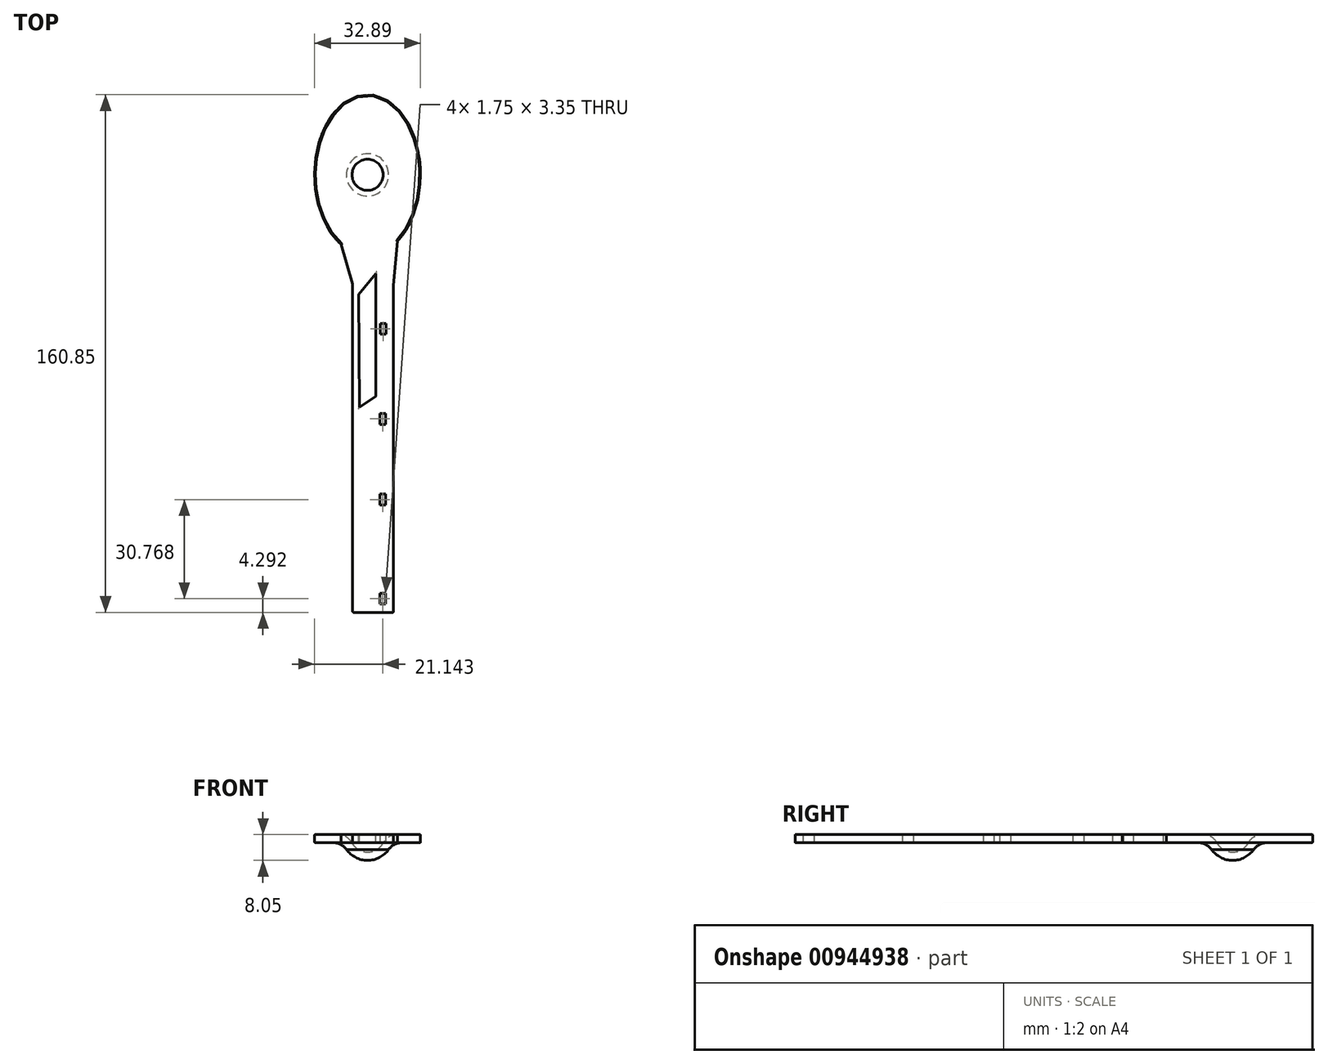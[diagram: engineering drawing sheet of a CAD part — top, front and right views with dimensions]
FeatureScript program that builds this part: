
annotation { "Feature Type Name" : "Feature", "Feature Type Description" : "" }
export const myFeature = defineFeature(function(context is Context, id is Id, definition is map)
    precondition{}
    {
        {
            var Q0;
            Q0=qCreatedBy(makeId("Top.planeOp"),FACE);
            var sketch = newSketch(context, id + "F0", { "sketchPlane" : qUnion([Q0])});
            skEllipticalArc(sketch, "E0", {});
            skLineSegment(sketch, "E1", {"start": v(-8.18, -21.6) * mm, "end": v(-4.62, -33.9) * mm});
            skLineSegment(sketch, "E2", {"start": v(-4.62, -33.9) * mm, "end": v(-4.62, -135.94) * mm});
            skLineSegment(sketch, "E3", {"start": v(-4.62, -135.94) * mm, "end": v(8.08, -135.94) * mm});
            skLineSegment(sketch, "E4", {"start": v(8.08, -135.94) * mm, "end": v(8.08, -34.34) * mm});
            skLineSegment(sketch, "E5", {"start": v(8.08, -34.34) * mm, "end": v(9.27, -20.58) * mm});
            const initialGuessF0  = {"E0": [0, 0, 0, -1, 0.0249080586106296, 0.0164429262639253, 0.5987226395592762, 5.762282687151485]};
            skSetInitialGuess(sketch, initialGuessF0);
            skSolve(sketch);
        }
        {
            var Q0;
            Q0 = qSketchRegion(id + "F0", true);
            extrude(context, id + "F1", {"entities" : qUnion([Q0]), "depth" : 2.54 * mm, "offsetDistance" : 25.4 * mm});
        }
        {
            var Q0;
            Q0=makeQuery(id+"F1.opExtrude","CAP_EDGE",EDGE,{"disambiguationData":[OSD([sQuery(id+"F0.wireOp",EDGE,"E1")])],"isStart":false});
            var Q1;
            Q1=makeQuery(id+"F1.opExtrude","CAP_EDGE",EDGE,{"disambiguationData":[OSD([sQuery(id+"F0.wireOp",EDGE,"E2")])],"isStart":false});
            var Q2;
            Q2=makeQuery(id+"F1.opExtrude","CAP_EDGE",EDGE,{"disambiguationData":[OSD([sQuery(id+"F0.wireOp",EDGE,"E0")])],"isStart":false});
            var Q3;
            Q3=makeQuery(id+"F1.opExtrude","CAP_EDGE",EDGE,{"disambiguationData":[OSD([sQuery(id+"F0.wireOp",EDGE,"E5")])],"isStart":false});
            var Q4;
            Q4=makeQuery(id+"F1.opExtrude","CAP_EDGE",EDGE,{"disambiguationData":[OSD([sQuery(id+"F0.wireOp",EDGE,"E4")])],"isStart":false});
            var Q5;
            Q5=makeQuery(id+"F1.opExtrude","CAP_EDGE",EDGE,{"disambiguationData":[OSD([sQuery(id+"F0.wireOp",EDGE,"E0")])],"isStart":true});
            var Q6;
            Q6=makeQuery(id+"F1.opExtrude","CAP_EDGE",EDGE,{"disambiguationData":[OSD([sQuery(id+"F0.wireOp",EDGE,"E5")])],"isStart":true});
            var Q7;
            Q7=makeQuery(id+"F1.opExtrude","CAP_EDGE",EDGE,{"disambiguationData":[OSD([sQuery(id+"F0.wireOp",EDGE,"E3")])],"isStart":true});
            var Q8;
            Q8=makeQuery(id+"F1.opExtrude","SWEPT_EDGE",EDGE,{"disambiguationData":[OSD([sQuery(id+"F0.wireOp",EDGE,"E3"),sQuery(id+"F0.wireOp",EDGE,"E4")])]});
            var Q9;
            Q9=makeQuery(id+"F1.opExtrude","CAP_EDGE",EDGE,{"disambiguationData":[OSD([sQuery(id+"F0.wireOp",EDGE,"E3")])],"isStart":false});
            var Q10;
            Q10=makeQuery(id+"F1.opExtrude","SWEPT_EDGE",EDGE,{"disambiguationData":[OSD([sQuery(id+"F0.wireOp",EDGE,"E2"),sQuery(id+"F0.wireOp",EDGE,"E3")])]});
            var Q11;
            Q11=makeQuery(id+"F1.opExtrude","CAP_EDGE",EDGE,{"disambiguationData":[OSD([sQuery(id+"F0.wireOp",EDGE,"E4")])],"isStart":true});
            fillet(context, id + "F2", {"entities" : qUnion([Q0, Q1, Q2, Q3, Q4, Q5, Q6, Q7, Q8, Q9, Q10, Q11]), "radius" : 0.25 * mm, "tangentPropagation" : true, "allowEdgeOverflow" : false});
        }
        {
            var Q0;
            Q0=makeQuery(id+"F1.opExtrude","CAP_FACE",FACE,{"disambiguationData":[OSD([sQuery(id+"F0.wireOp",EDGE,"E0"),sQuery(id+"F0.wireOp",EDGE,"E1"),sQuery(id+"F0.wireOp",EDGE,"E2"),sQuery(id+"F0.wireOp",EDGE,"E3"),sQuery(id+"F0.wireOp",EDGE,"E4"),sQuery(id+"F0.wireOp",EDGE,"E5")])],"isStart":false});
            var sketch = newSketch(context, id + "F3", { "sketchPlane" : qUnion([Q0])});
            skLineSegment(sketch, "E6", {"start": v(-2.5, -72.22) * mm, "end": v(2.5, -68.83) * mm});
            skLineSegment(sketch, "E7", {"start": v(2.5, -68.83) * mm, "end": v(2.5, -30.73) * mm});
            skLineSegment(sketch, "E8", {"start": v(2.5, -30.73) * mm, "end": v(-2.82, -37.19) * mm});
            skLineSegment(sketch, "E9", {"start": v(-2.82, -37.19) * mm, "end": v(-2.5, -72.22) * mm});
            skSolve(sketch);
        }
        {
            var Q0;
            Q0 = qSketchRegion(id + "F3", true);
            extrude(context, id + "F4", {"entities" : qUnion([Q0]), "operationType" : NewBodyOperationType.REMOVE, "oppositeDirection" : true, "depth" : 25.4 * mm, "offsetDistance" : 25.4 * mm});
        }
        {
            var Q0;
            Q0=makeQuery(id+"F4.boolean.opBoolean","COPY",EDGE,{"derivedFrom":makeQuery(id+"F4.opExtrude","CAP_EDGE",EDGE,{"disambiguationData":[OSD([sQuery(id+"F3.wireOp",EDGE,"E8")])],"isStart":true})});
            var Q1;
            Q1=makeQuery(id+"F4.boolean.opBoolean","COPY",EDGE,{"derivedFrom":makeQuery(id+"F4.opExtrude","CAP_EDGE",EDGE,{"disambiguationData":[OSD([sQuery(id+"F3.wireOp",EDGE,"E9")])],"isStart":true})});
            var Q2;
            Q2=makeQuery(id+"F4.boolean.opBoolean","COPY",EDGE,{"derivedFrom":makeQuery(id+"F4.opExtrude","CAP_EDGE",EDGE,{"disambiguationData":[OSD([sQuery(id+"F3.wireOp",EDGE,"E7")])],"isStart":true})});
            var Q3;
            Q3=makeQuery(id+"F4.boolean.opBoolean","COPY",EDGE,{"derivedFrom":makeQuery(id+"F4.opExtrude","CAP_EDGE",EDGE,{"disambiguationData":[OSD([sQuery(id+"F3.wireOp",EDGE,"E6")])],"isStart":true})});
            var Q4;
            Q4=makeQuery(id+"F4.boolean.opBoolean","INTERSECT",EDGE,{"derivedFrom":[makeQuery(id+"F1.opExtrude","CAP_FACE",FACE,{"disambiguationData":[OSD([sQuery(id+"F0.wireOp",EDGE,"E0"),sQuery(id+"F0.wireOp",EDGE,"E1"),sQuery(id+"F0.wireOp",EDGE,"E2"),sQuery(id+"F0.wireOp",EDGE,"E3"),sQuery(id+"F0.wireOp",EDGE,"E4"),sQuery(id+"F0.wireOp",EDGE,"E5")])],"isStart":true}),makeQuery(id+"F4.opExtrude","SWEPT_FACE",FACE,{"disambiguationData":[OSD([sQuery(id+"F3.wireOp",EDGE,"E8")])]})]});
            var Q5;
            Q5=makeQuery(id+"F4.boolean.opBoolean","INTERSECT",EDGE,{"derivedFrom":[makeQuery(id+"F1.opExtrude","CAP_FACE",FACE,{"disambiguationData":[OSD([sQuery(id+"F0.wireOp",EDGE,"E0"),sQuery(id+"F0.wireOp",EDGE,"E1"),sQuery(id+"F0.wireOp",EDGE,"E2"),sQuery(id+"F0.wireOp",EDGE,"E3"),sQuery(id+"F0.wireOp",EDGE,"E4"),sQuery(id+"F0.wireOp",EDGE,"E5")])],"isStart":true}),makeQuery(id+"F4.opExtrude","SWEPT_FACE",FACE,{"disambiguationData":[OSD([sQuery(id+"F3.wireOp",EDGE,"E7")])]})]});
            var Q6;
            Q6=makeQuery(id+"F4.boolean.opBoolean","INTERSECT",EDGE,{"derivedFrom":[makeQuery(id+"F1.opExtrude","CAP_FACE",FACE,{"disambiguationData":[OSD([sQuery(id+"F0.wireOp",EDGE,"E0"),sQuery(id+"F0.wireOp",EDGE,"E1"),sQuery(id+"F0.wireOp",EDGE,"E2"),sQuery(id+"F0.wireOp",EDGE,"E3"),sQuery(id+"F0.wireOp",EDGE,"E4"),sQuery(id+"F0.wireOp",EDGE,"E5")])],"isStart":true}),makeQuery(id+"F4.opExtrude","SWEPT_FACE",FACE,{"disambiguationData":[OSD([sQuery(id+"F3.wireOp",EDGE,"E9")])]})]});
            var Q7;
            Q7=makeQuery(id+"F4.boolean.opBoolean","INTERSECT",EDGE,{"derivedFrom":[makeQuery(id+"F1.opExtrude","CAP_FACE",FACE,{"disambiguationData":[OSD([sQuery(id+"F0.wireOp",EDGE,"E0"),sQuery(id+"F0.wireOp",EDGE,"E1"),sQuery(id+"F0.wireOp",EDGE,"E2"),sQuery(id+"F0.wireOp",EDGE,"E3"),sQuery(id+"F0.wireOp",EDGE,"E4"),sQuery(id+"F0.wireOp",EDGE,"E5")])],"isStart":true}),makeQuery(id+"F4.opExtrude","SWEPT_FACE",FACE,{"disambiguationData":[OSD([sQuery(id+"F3.wireOp",EDGE,"E6")])]})]});
            fillet(context, id + "F5", {"entities" : qUnion([Q0, Q1, Q2, Q3, Q4, Q5, Q6, Q7]), "radius" : 0.25 * mm, "tangentPropagation" : true, "allowEdgeOverflow" : false});
        }
        {
            var Q0;
            Q0=makeQuery(id+"F1.opExtrude","CAP_FACE",FACE,{"disambiguationData":[OSD([sQuery(id+"F0.wireOp",EDGE,"E0"),sQuery(id+"F0.wireOp",EDGE,"E1"),sQuery(id+"F0.wireOp",EDGE,"E2"),sQuery(id+"F0.wireOp",EDGE,"E3"),sQuery(id+"F0.wireOp",EDGE,"E4"),sQuery(id+"F0.wireOp",EDGE,"E5")])],"isStart":false});
            var sketch = newSketch(context, id + "F6", { "sketchPlane" : qUnion([Q0])});
            skArc(sketch, "E10", {"start": v(-8.05, 0) * mm, "mid": v(0, -8.05) * mm, "end": v(8.05, 0) * mm});
            skLineSegment(sketch, "E11", {"start": v(-8.05, 0) * mm, "end": v(8.05, 0) * mm});
            skSolve(sketch);
        }
        {
            var Q0;
            Q0=makeQuery(id+"F6.imprint","IMPRINT",FACE,{"disambiguationData":[TD([[makeQuery(id+"F6.imprint","IMPRINT",EDGE,{"derivedFrom":sQuery(id+"F6.wireOp",EDGE,"E10")}),1.0]])]});
            var Q1;
            Q1=sQuery(id+"F6.wireOp",EDGE,"E11");
            revolve(context, id + "F7", {"operationType" : NewBodyOperationType.ADD, "surfaceOperationType" : NewSurfaceOperationType.NEW, "entities" : qUnion([Q0]), "axis" : qUnion([Q1]), "revolveType" : RevolveType.FULL});
        }
        {
            var Q0;
            Q0=qCreatedBy(makeId("Top.planeOp"),FACE);
            cPlane(context, id + "F8", {"entities" : qUnion([Q0]), "cplaneType" : CPlaneType.OFFSET, "offset" : 2.54 * mm, "width" : 152.4 * mm, "height" : 152.4 * mm});
        }
        {
            var Q0;
            Q0=qCreatedBy(id+"F8.planeOp",FACE);
            var sketch = newSketch(context, id + "F9", { "sketchPlane" : qUnion([Q0])});
            skLineSegment(sketch, "E12.bottom", {"start": v(-10.65, -8.66) * mm, "end": v(10.65, -8.66) * mm});
            skLineSegment(sketch, "E12.top", {"start": v(-10.65, 8.66) * mm, "end": v(10.65, 8.66) * mm});
            skLineSegment(sketch, "E12.left", {"start": v(-10.65, -8.66) * mm, "end": v(-10.65, 8.66) * mm});
            skLineSegment(sketch, "E12.right", {"start": v(10.65, -8.66) * mm, "end": v(10.65, 8.66) * mm});
            skPoint(sketch, "E12.middle", {"position": v(0, 0) * mm});
            skSolve(sketch);
        }
        {
            var Q0;
            Q0 = qSketchRegion(id + "F9", true);
            extrude(context, id + "F10", {"entities" : qUnion([Q0]), "operationType" : NewBodyOperationType.REMOVE, "depth" : 25.4 * mm, "offsetDistance" : 25.4 * mm});
        }
        {
            var Q0;
            Q0=makeQuery(id+"F10.boolean.opBoolean","MERGE",FACE,{"derivedFrom":[makeQuery(id+"F1.opExtrude","CAP_FACE",FACE,{"disambiguationData":[OSD([sQuery(id+"F0.wireOp",EDGE,"E0"),sQuery(id+"F0.wireOp",EDGE,"E1"),sQuery(id+"F0.wireOp",EDGE,"E2"),sQuery(id+"F0.wireOp",EDGE,"E3"),sQuery(id+"F0.wireOp",EDGE,"E4"),sQuery(id+"F0.wireOp",EDGE,"E5")])],"isStart":false})],"fromTools":[makeQuery(id+"F10.opExtrude","CAP_FACE",FACE,{"disambiguationData":[OSD([sQuery(id+"F9.wireOp",EDGE,"E12.bottom"),sQuery(id+"F9.wireOp",EDGE,"E12.top"),sQuery(id+"F9.wireOp",EDGE,"E12.left"),sQuery(id+"F9.wireOp",EDGE,"E12.right")])],"isStart":true})]});
            shell(context, id + "F11", {"entities" : qUnion([Q0]), "thickness" : 2.54 * mm});
        }
        {
            var Q0;
            Q0=makeQuery(id+"F7.boolean.opBoolean","INTERSECT",EDGE,{"derivedFrom":[makeQuery(id+"F1.opExtrude","CAP_FACE",FACE,{"disambiguationData":[OSD([sQuery(id+"F0.wireOp",EDGE,"E0"),sQuery(id+"F0.wireOp",EDGE,"E1"),sQuery(id+"F0.wireOp",EDGE,"E2"),sQuery(id+"F0.wireOp",EDGE,"E3"),sQuery(id+"F0.wireOp",EDGE,"E4"),sQuery(id+"F0.wireOp",EDGE,"E5")])],"isStart":true}),makeQuery(id+"F7.opRevolve","SWEPT_FACE",FACE,{"disambiguationData":[OSD([sQuery(id+"F6.wireOp",EDGE,"E10")])]})]});
            fillet(context, id + "F12", {"entities" : qUnion([Q0]), "radius" : 5.08 * mm, "tangentPropagation" : true, "allowEdgeOverflow" : false});
        }
        {
            var Q0;
            Q0=makeQuery(id+"F11.opShell","OFFSET_EDGE",EDGE,{"disambiguationData":[OSD([sQuery(id+"F0.wireOp",EDGE,"E0"),sQuery(id+"F0.wireOp",EDGE,"E1"),sQuery(id+"F0.wireOp",EDGE,"E2"),sQuery(id+"F0.wireOp",EDGE,"E3"),sQuery(id+"F0.wireOp",EDGE,"E4"),sQuery(id+"F0.wireOp",EDGE,"E5"),sQuery(id+"F6.wireOp",EDGE,"E10")])]});
            fillet(context, id + "F13", {"entities" : qUnion([Q0]), "radius" : 5.08 * mm, "tangentPropagation" : true, "allowEdgeOverflow" : false});
        }
        {
            var Q0;
            Q0=makeQuery(id+"F10.boolean.opBoolean","MERGE",FACE,{"derivedFrom":[makeQuery(id+"F1.opExtrude","CAP_FACE",FACE,{"disambiguationData":[OSD([sQuery(id+"F0.wireOp",EDGE,"E0"),sQuery(id+"F0.wireOp",EDGE,"E1"),sQuery(id+"F0.wireOp",EDGE,"E2"),sQuery(id+"F0.wireOp",EDGE,"E3"),sQuery(id+"F0.wireOp",EDGE,"E4"),sQuery(id+"F0.wireOp",EDGE,"E5")])],"isStart":false})],"fromTools":[makeQuery(id+"F10.opExtrude","CAP_FACE",FACE,{"disambiguationData":[OSD([sQuery(id+"F9.wireOp",EDGE,"E12.bottom"),sQuery(id+"F9.wireOp",EDGE,"E12.top"),sQuery(id+"F9.wireOp",EDGE,"E12.left"),sQuery(id+"F9.wireOp",EDGE,"E12.right")])],"isStart":true})]});
            var sketch = newSketch(context, id + "F14", { "sketchPlane" : qUnion([Q0])});
            skLineSegment(sketch, "E13.bottom", {"start": v(5.7, -49.49) * mm, "end": v(3.96, -49.49) * mm});
            skLineSegment(sketch, "E13.top", {"start": v(5.7, -46.13) * mm, "end": v(3.96, -46.13) * mm});
            skLineSegment(sketch, "E13.left", {"start": v(5.7, -49.49) * mm, "end": v(5.7, -46.13) * mm});
            skLineSegment(sketch, "E13.right", {"start": v(3.96, -49.49) * mm, "end": v(3.96, -46.13) * mm});
            skPoint(sketch, "E13.middle", {"position": v(4.83, -47.8) * mm});
            skSolve(sketch);
        }
        {
            var Q0;
            Q0=makeQuery(id+"F1.opExtrude","CAP_FACE",FACE,{"disambiguationData":[OSD([sQuery(id+"F0.wireOp",EDGE,"E0"),sQuery(id+"F0.wireOp",EDGE,"E1"),sQuery(id+"F0.wireOp",EDGE,"E2"),sQuery(id+"F0.wireOp",EDGE,"E3"),sQuery(id+"F0.wireOp",EDGE,"E4"),sQuery(id+"F0.wireOp",EDGE,"E5")])],"isStart":true});
            var sketch = newSketch(context, id + "F15", { "sketchPlane" : qUnion([Q0])});
            skLineSegment(sketch, "E14", {"start": v(5.57, 46.08) * mm, "end": v(5.57, 122.36) * mm});
            skLineSegment(sketch, "E15.bottom", {"start": v(5.57, 74.16) * mm, "end": v(3.82, 74.16) * mm});
            skLineSegment(sketch, "E15.top", {"start": v(5.57, 77.51) * mm, "end": v(3.82, 77.51) * mm});
            skLineSegment(sketch, "E15.left", {"start": v(5.57, 74.16) * mm, "end": v(5.57, 77.51) * mm});
            skLineSegment(sketch, "E15.right", {"start": v(3.82, 74.16) * mm, "end": v(3.82, 77.51) * mm});
            skLineSegment(sketch, "E16.bottom", {"start": v(5.57, 102.56) * mm, "end": v(3.82, 102.56) * mm});
            skLineSegment(sketch, "E16.top", {"start": v(5.57, 99.2) * mm, "end": v(3.82, 99.2) * mm});
            skLineSegment(sketch, "E16.left", {"start": v(5.57, 102.56) * mm, "end": v(5.57, 99.2) * mm});
            skLineSegment(sketch, "E16.right", {"start": v(3.82, 102.56) * mm, "end": v(3.82, 99.2) * mm});
            skSolve(sketch);
        }
        {
            var Q0;
            Q0 = qSketchRegion(id + "F14", true);
            extrude(context, id + "F16", {"entities" : qUnion([Q0]), "operationType" : NewBodyOperationType.REMOVE, "oppositeDirection" : true, "depth" : 25.4 * mm, "offsetDistance" : 25.4 * mm});
        }
        {
            var Q0;
            Q0 = qSketchRegion(id + "F15", true);
            extrude(context, id + "F17", {"entities" : qUnion([Q0]), "operationType" : NewBodyOperationType.REMOVE, "oppositeDirection" : true, "depth" : 25.4 * mm, "offsetDistance" : 25.4 * mm});
        }
        {
            var Q0;
            Q0=makeQuery(id+"F10.boolean.opBoolean","MERGE",FACE,{"derivedFrom":[makeQuery(id+"F1.opExtrude","CAP_FACE",FACE,{"disambiguationData":[OSD([sQuery(id+"F0.wireOp",EDGE,"E0"),sQuery(id+"F0.wireOp",EDGE,"E1"),sQuery(id+"F0.wireOp",EDGE,"E2"),sQuery(id+"F0.wireOp",EDGE,"E3"),sQuery(id+"F0.wireOp",EDGE,"E4"),sQuery(id+"F0.wireOp",EDGE,"E5")])],"isStart":false})],"fromTools":[makeQuery(id+"F10.opExtrude","CAP_FACE",FACE,{"disambiguationData":[OSD([sQuery(id+"F9.wireOp",EDGE,"E12.bottom"),sQuery(id+"F9.wireOp",EDGE,"E12.top"),sQuery(id+"F9.wireOp",EDGE,"E12.left"),sQuery(id+"F9.wireOp",EDGE,"E12.right")])],"isStart":true})]});
            var sketch = newSketch(context, id + "F18", { "sketchPlane" : qUnion([Q0])});
            skLineSegment(sketch, "E17", {"start": v(5.57, -99.2) * mm, "end": v(5.57, -133.32) * mm});
            skLineSegment(sketch, "E18.bottom", {"start": v(5.57, -133.32) * mm, "end": v(3.82, -133.32) * mm});
            skLineSegment(sketch, "E18.top", {"start": v(5.57, -129.97) * mm, "end": v(3.82, -129.97) * mm});
            skLineSegment(sketch, "E18.left", {"start": v(5.57, -133.32) * mm, "end": v(5.57, -129.97) * mm});
            skLineSegment(sketch, "E18.right", {"start": v(3.82, -133.32) * mm, "end": v(3.82, -129.97) * mm});
            skSolve(sketch);
        }
        {
            var Q0;
            Q0 = qSketchRegion(id + "F18", true);
            extrude(context, id + "F19", {"entities" : qUnion([Q0]), "operationType" : NewBodyOperationType.REMOVE, "oppositeDirection" : true, "depth" : 25.4 * mm, "offsetDistance" : 25.4 * mm});
        }
    });
